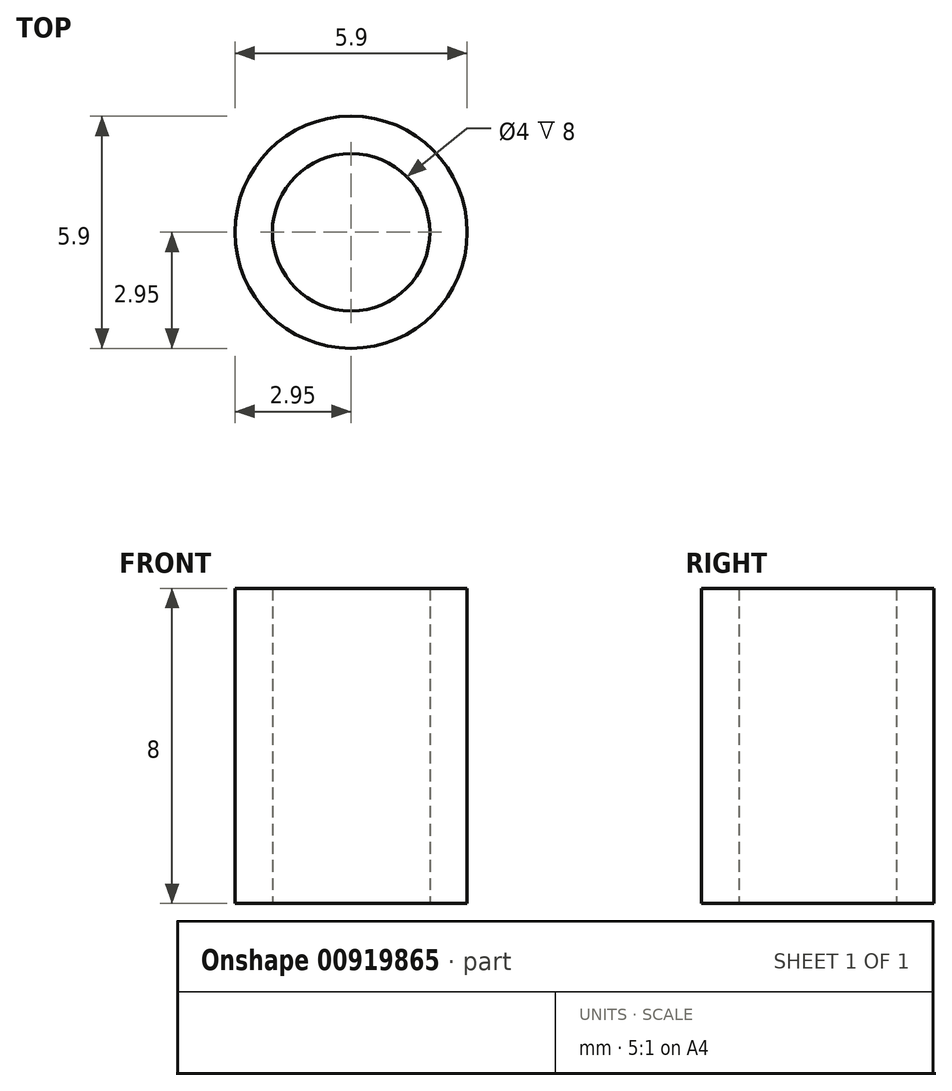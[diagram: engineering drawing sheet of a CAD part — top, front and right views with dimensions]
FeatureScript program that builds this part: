
annotation { "Feature Type Name" : "Feature", "Feature Type Description" : "" }
export const myFeature = defineFeature(function(context is Context, id is Id, definition is map)
    precondition{}
    {
        {
            var Q0;
            Q0=qCreatedBy(makeId("Top.planeOp"),FACE);
            var sketch = newSketch(context, id + "F0", { "sketchPlane" : qUnion([Q0])});
            skCircle(sketch, "E0", {"center": v(0, 0) * mm, "radius": 2.95 * mm});
            skCircle(sketch, "E1", {"center": v(0, 0) * mm, "radius": 2 * mm});
            skSolve(sketch);
        }
        {
            var Q0;
            Q0=makeQuery(id+"F0.imprint","IMPRINT",FACE,{"disambiguationData":[TD([[makeQuery(id+"F0.imprint","IMPRINT",EDGE,{"derivedFrom":sQuery(id+"F0.wireOp",EDGE,"E0")}),1.0]])]});
            extrude(context, id + "F1", {"entities" : qUnion([Q0]), "depth" : 8 * mm, "offsetDistance" : 25 * mm});
        }
    });
